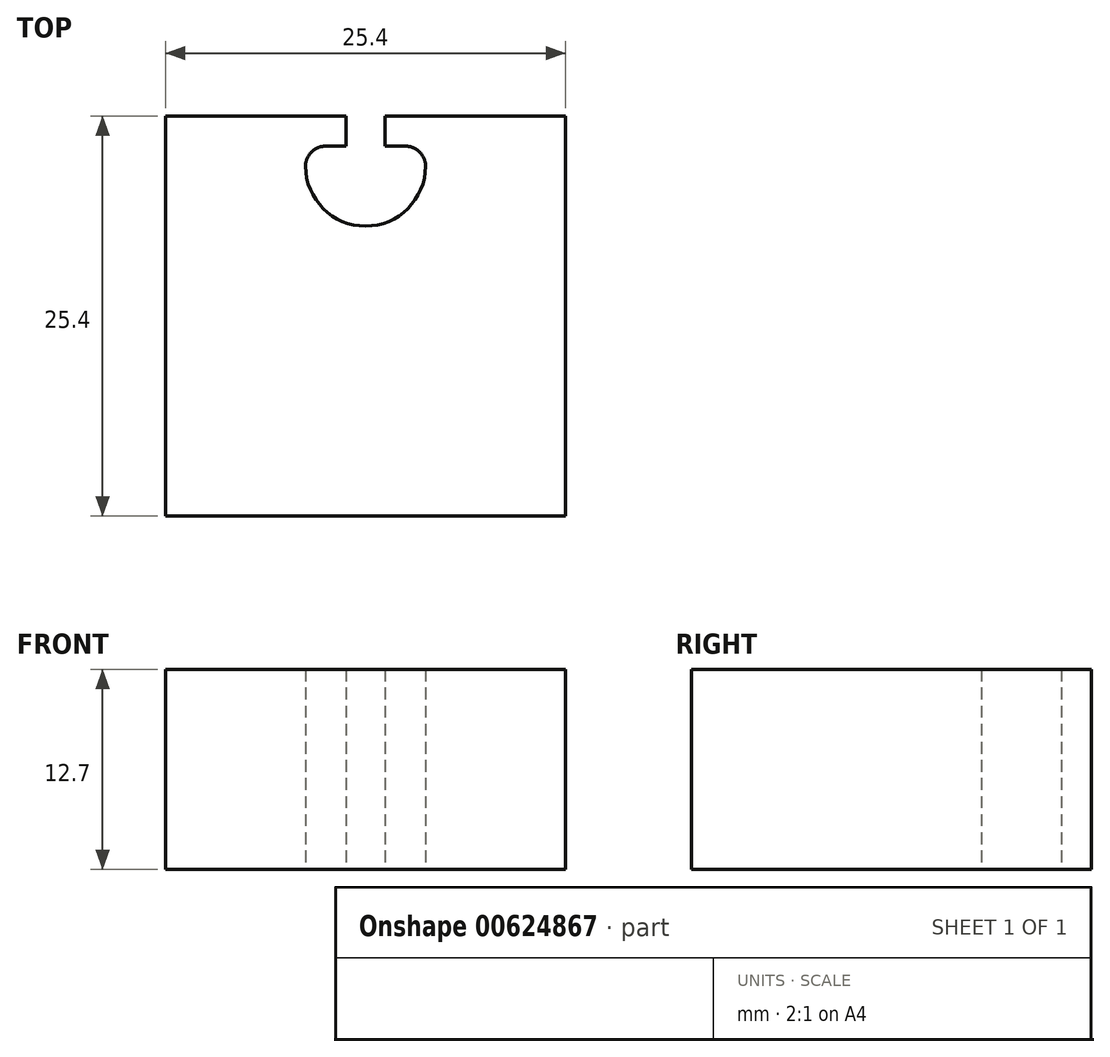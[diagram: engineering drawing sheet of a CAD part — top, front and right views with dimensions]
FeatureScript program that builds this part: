
annotation { "Feature Type Name" : "Feature", "Feature Type Description" : "" }
export const myFeature = defineFeature(function(context is Context, id is Id, definition is map)
    precondition{}
    {
        {
            var Q0;
            Q0=qCreatedBy(makeId("Top.planeOp"),FACE);
            var sketch = newSketch(context, id + "F0", { "sketchPlane" : qUnion([Q0])});
            skLineSegment(sketch, "E0.top", {"start": v(-12.7, -12.7) * mm, "end": v(12.7, -12.7) * mm});
            skLineSegment(sketch, "E0.left", {"start": v(-12.7, 12.7) * mm, "end": v(-12.7, -12.7) * mm});
            skLineSegment(sketch, "E0.right", {"start": v(12.7, 12.7) * mm, "end": v(12.7, -12.7) * mm});
            skPoint(sketch, "E0.middle", {"position": v(0, 0) * mm});
            skPoint(sketch, "E1.center.orphan", {"position": v(0, 9.53) * mm});
            skArc(sketch, "E2", {"start": v(-3.81, 9.52) * mm, "mid": v(0, 5.71) * mm, "end": v(3.81, 9.52) * mm});
            skLineSegment(sketch, "E3", {"start": v(0, 9.53) * mm, "end": v(-10, 9.53) * mm, "construction": true});
            skLineSegment(sketch, "E4", {"start": v(0, 9.53) * mm, "end": v(9.23, 9.53) * mm, "construction": true});
            skLineSegment(sketch, "E5", {"start": v(-12.7, 12.7) * mm, "end": v(-1.25, 12.7) * mm});
            skLineSegment(sketch, "E6", {"start": v(-1.25, 12.7) * mm, "end": v(-1.25, 10.79) * mm});
            skLineSegment(sketch, "E7", {"start": v(-1.25, 10.79) * mm, "end": v(-3.81, 10.79) * mm});
            skLineSegment(sketch, "E8", {"start": v(-3.81, 9.52) * mm, "end": v(-3.81, 10.79) * mm});
            skLineSegment(sketch, "E9.MirrorCS", {"start": v(12.7, 12.7) * mm, "end": v(1.25, 12.7) * mm});
            skLineSegment(sketch, "E10.MirrorCS", {"start": v(1.25, 12.7) * mm, "end": v(1.25, 10.79) * mm});
            skLineSegment(sketch, "E11.MirrorCS", {"start": v(1.25, 10.79) * mm, "end": v(3.81, 10.79) * mm});
            skLineSegment(sketch, "E12.MirrorCS", {"start": v(3.81, 9.52) * mm, "end": v(3.81, 10.79) * mm});
            skSolve(sketch);
        }
        {
            var Q0;
            Q0 = qSketchRegion(id + "F0", true);
            extrude(context, id + "F1", {"entities" : qUnion([Q0]), "endBound" : BoundingType.SYMMETRIC, "depth" : 12.7 * mm, "offsetDistance" : 25.4 * mm});
        }
        {
            var Q0;
            Q0=makeQuery(id+"F1.opExtrude","SWEPT_EDGE",EDGE,{"disambiguationData":[OSD([sQuery(id+"F0.wireOp",EDGE,"E7"),sQuery(id+"F0.wireOp",EDGE,"E8")])]});
            var Q1;
            Q1=makeQuery(id+"F1.opExtrude","SWEPT_EDGE",EDGE,{"disambiguationData":[OSD([sQuery(id+"F0.wireOp",EDGE,"E11.MirrorCS"),sQuery(id+"F0.wireOp",EDGE,"E12.MirrorCS")])]});
            fillet(context, id + "F2", {"entities" : qUnion([Q0, Q1]), "radius" : 1.27 * mm, "tangentPropagation" : true, "allowEdgeOverflow" : false});
        }
    });
